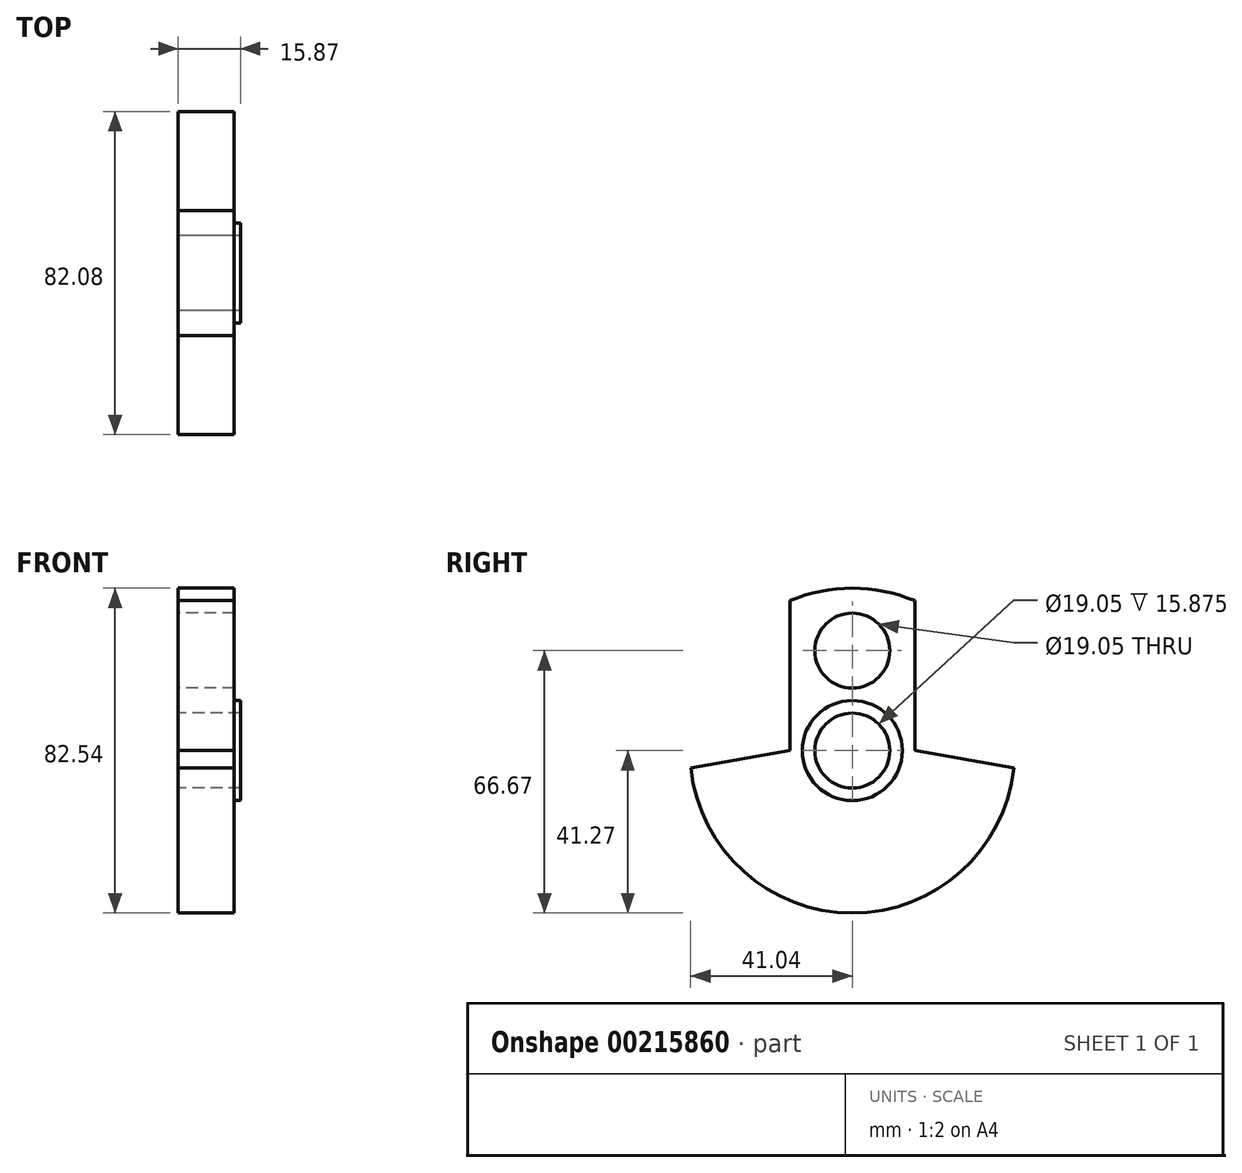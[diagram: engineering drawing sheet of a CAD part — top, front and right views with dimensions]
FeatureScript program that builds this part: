
annotation { "Feature Type Name" : "Feature", "Feature Type Description" : "" }
export const myFeature = defineFeature(function(context is Context, id is Id, definition is map)
    precondition{}
    {
        {
            var Q0;
            Q0=qCreatedBy(makeId("Right.planeOp"),FACE);
            var sketch = newSketch(context, id + "F0", { "sketchPlane" : qUnion([Q0])});
            skArc(sketch, "E0", {"start": v(-41.04, -4.44) * mm, "mid": v(0, -41.27) * mm, "end": v(41.04, -4.44) * mm});
            skArc(sketch, "E1", {"start": v(-15.87, 38.1) * mm, "mid": v(0, 41.28) * mm, "end": v(15.88, 38.1) * mm});
            skLineSegment(sketch, "E2", {"start": v(-15.88, 38.1) * mm, "end": v(-15.87, 0) * mm});
            skLineSegment(sketch, "E3", {"start": v(-15.87, 0) * mm, "end": v(-41.04, -4.44) * mm});
            skLineSegment(sketch, "E4", {"start": v(15.87, 38.1) * mm, "end": v(15.88, 0) * mm});
            skLineSegment(sketch, "E5", {"start": v(15.87, 0) * mm, "end": v(41.04, -4.44) * mm});
            skCircle(sketch, "E6", {"center": v(0, 0) * mm, "radius": 9.53 * mm});
            skCircle(sketch, "E7", {"center": v(0, 25.4) * mm, "radius": 9.53 * mm});
            skSolve(sketch);
        }
        {
            var Q0;
            Q0=qSketchRegion(id+"F0",true);
            extrude(context, id + "F1", {"entities" : qUnion([Q0]), "endBound" : BoundingType.SYMMETRIC, "depth" : 14.29 * mm});
        }
        {
            var Q0;
            Q0=makeQuery(id+"F1.opExtrude","CAP_FACE",FACE,{"disambiguationData":[OSD([sQuery(id+"F0.wireOp",EDGE,"E0"),sQuery(id+"F0.wireOp",EDGE,"E1"),sQuery(id+"F0.wireOp",EDGE,"E2"),sQuery(id+"F0.wireOp",EDGE,"E3"),sQuery(id+"F0.wireOp",EDGE,"E4"),sQuery(id+"F0.wireOp",EDGE,"E5"),sQuery(id+"F0.wireOp",EDGE,"E6"),sQuery(id+"F0.wireOp",EDGE,"E7")])],"isStart":false});
            var sketch = newSketch(context, id + "F2", { "sketchPlane" : qUnion([Q0])});
            skCircle(sketch, "E8", {"center": v(0, 0) * mm, "radius": 12.7 * mm});
            skSolve(sketch);
        }
        {
            var Q0;
            Q0=makeQuery(id+"F2.imprint","IMPRINT",FACE,{"disambiguationData":[TD([[makeQuery(id+"F2.imprint","IMPRINT",EDGE,{"derivedFrom":sQuery(id+"F2.wireOp",EDGE,"E8")}),1.0]])]});
            extrude(context, id + "F3", {"entities" : qUnion([Q0]), "operationType" : NewBodyOperationType.ADD, "depth" : 1.59 * mm});
        }
    });
